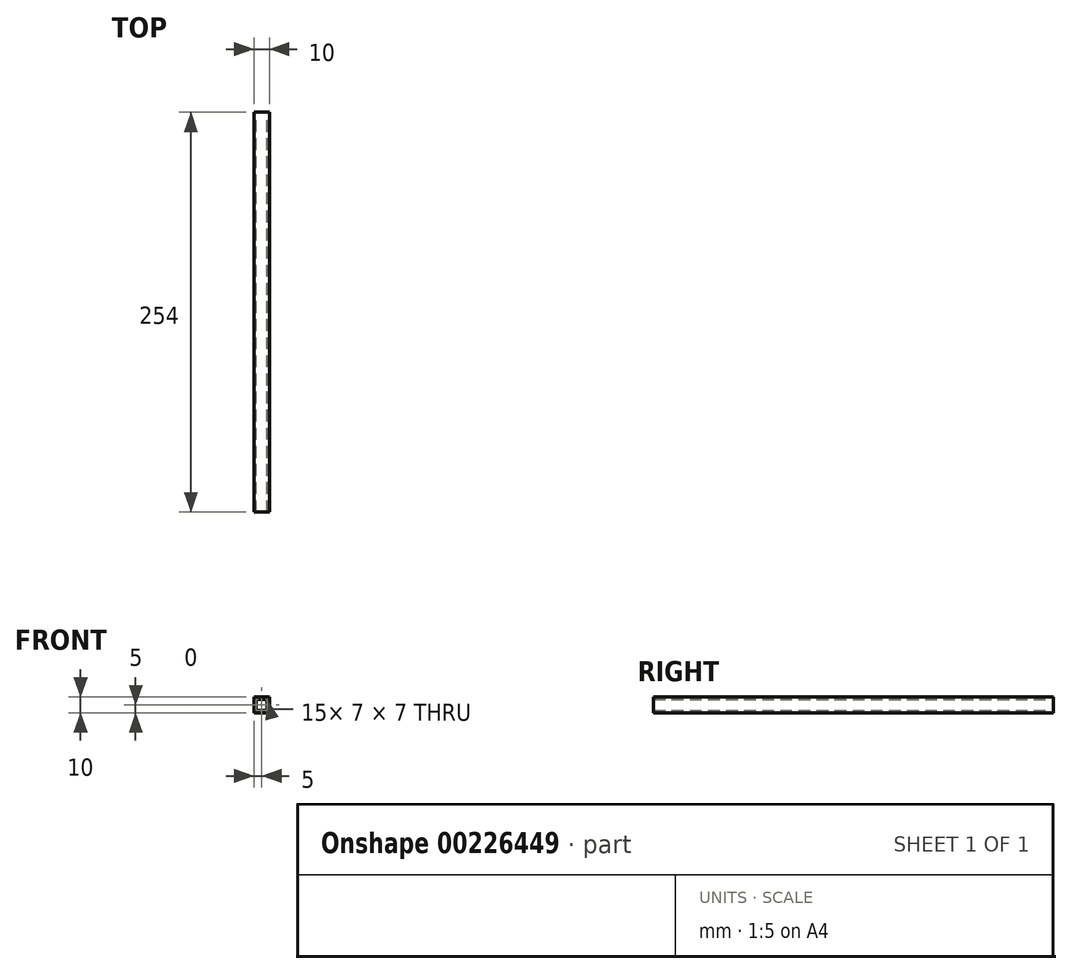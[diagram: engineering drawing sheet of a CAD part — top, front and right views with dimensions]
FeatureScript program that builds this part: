
annotation { "Feature Type Name" : "Feature", "Feature Type Description" : "" }
export const myFeature = defineFeature(function(context is Context, id is Id, definition is map)
    precondition{}
    {
        {
            var Q0;
            Q0=qCreatedBy(makeId("Front.planeOp"),FACE);
            var sketch = newSketch(context, id + "F0", { "sketchPlane" : qUnion([Q0])});
            skLineSegment(sketch, "E0.bottom", {"start": v(5, 5) * mm, "end": v(-5, 5) * mm});
            skLineSegment(sketch, "E0.top", {"start": v(5, -5) * mm, "end": v(-5, -5) * mm});
            skLineSegment(sketch, "E0.left", {"start": v(5, 5) * mm, "end": v(5, -5) * mm});
            skLineSegment(sketch, "E0.right", {"start": v(-5, 5) * mm, "end": v(-5, -5) * mm});
            skPoint(sketch, "E0.middle", {"position": v(0, 0) * mm});
            skLineSegment(sketch, "E1.bottom", {"start": v(3.5, 3.5) * mm, "end": v(-3.5, 3.5) * mm});
            skLineSegment(sketch, "E1.top", {"start": v(3.5, -3.5) * mm, "end": v(-3.5, -3.5) * mm});
            skLineSegment(sketch, "E1.left", {"start": v(3.5, 3.5) * mm, "end": v(3.5, -3.5) * mm});
            skLineSegment(sketch, "E1.right", {"start": v(-3.5, 3.5) * mm, "end": v(-3.5, -3.5) * mm});
            skSolve(sketch);
        }
        {
            var Q0;
            Q0=makeQuery(id+"F0.imprint","IMPRINT",FACE,{"disambiguationData":[TD([[makeQuery(id+"F0.imprint","IMPRINT",EDGE,{"derivedFrom":sQuery(id+"F0.wireOp",EDGE,"E0.bottom")}),1.0]])]});
            extrude(context, id + "F1", {"entities" : qUnion([Q0]), "depth" : 254 * mm, "offsetDistance" : 25.4 * mm});
        }
    });
